# Revit family: EKF_EE_ПанельПодППН_PROxima
name_source: partatom
category: Электрооборудование
units: mm (PartAtom-declared; Revit-internal decimal feet)

## family parameters
Всегда вертикально = Нет
На основе рабочей плоскости = Да
Общий = Да
При загрузке вырезать с полостями = Нет
Размер круглого соединителя = Использовать диаметр
Тип детали = Силовой щит
Точка расчета площади = Нет

## types (4) — shared parameters
ADSK_Единица измерения = шт.
ADSK_Завод-изготовитель = EKF
ADSK_Количество = 1
ADSK_Материал = Сталь_Оцинкованная
ADSK_Размер_Высота = 160 мм
ADSK_Размер_Глубина = 29 мм
D = 7 мм
T = 1 мм
Высота = 156 мм
Загиб1 = Да
Загиб1_Ширина = 29 мм
Загиб2_Ширина = 10 мм
Изготовитель = EKF
Отв_Кол = 2
Отступ = 16 мм
Серия номенклатуры = Unit PROxima
Степень защиты IP = -
ТВ = EKF_2
Тип установки = -
Шаг = 76 мм
zero-valued in all types: ADSK_Масса, Отметка по умолчанию

## per-type parameters (varying)
| type | ADSK_Код изделия | ADSK_Марка | ADSK_Обозначение | ADSK_Размер_Ширина | ОтвН_Кол | Отступ2 | Отступ_ОтвН | Тип |
| Панель под ППН к ВРУ Unit (Вх450хГ) EKF PROxima | mb15-08-01-07 | Панель под ППН к ВРУ Unit (Вх450хГ) | Панель под ППН к ВРУ Unit (Вх450хГ) | 360 мм | 4 | 11 мм | 66 мм | 64 мм |
| Панель под ППН к ВРУ Unit и ЩО-70 (Вх1000хГ) EKF PROxima | mb15-10-01-08 | Панель под ППН к ВРУ Unit и ЩО-70 (Вх1000хГ) | Панель под ППН к ВРУ Unit и ЩО-70 (Вх1000хГ) | 910 мм | 11 | 9 мм | 75 мм | 65 мм |
| Панель под ППН к ВРУ Unit и ЩО-70 (Вх600хГ) EKF PROxima | mb15-08-01-08 | Панель под ППН к ВРУ Unit и ЩО-70 (Вх600хГ) | Панель под ППН к ВРУ Unit и ЩО-70 (Вх600хГ) | 510 мм | 6 | 9 мм | 65 мм | 66 мм |
| Панель под ППН к ВРУ Unit и ЩО-70 (Вх800хГ) EKF PROxima | mb15-08-01-09 | Панель под ППН к ВРУ Unit и ЩО-70 (Вх800хГ) | Панель под ППН к ВРУ Unit и ЩО-70 (Вх800хГ) | 710 мм | 9 | 9 мм | 51 мм | 67 мм |

note: column(s) folded — value = type name in every type: ADSK_Наименование
